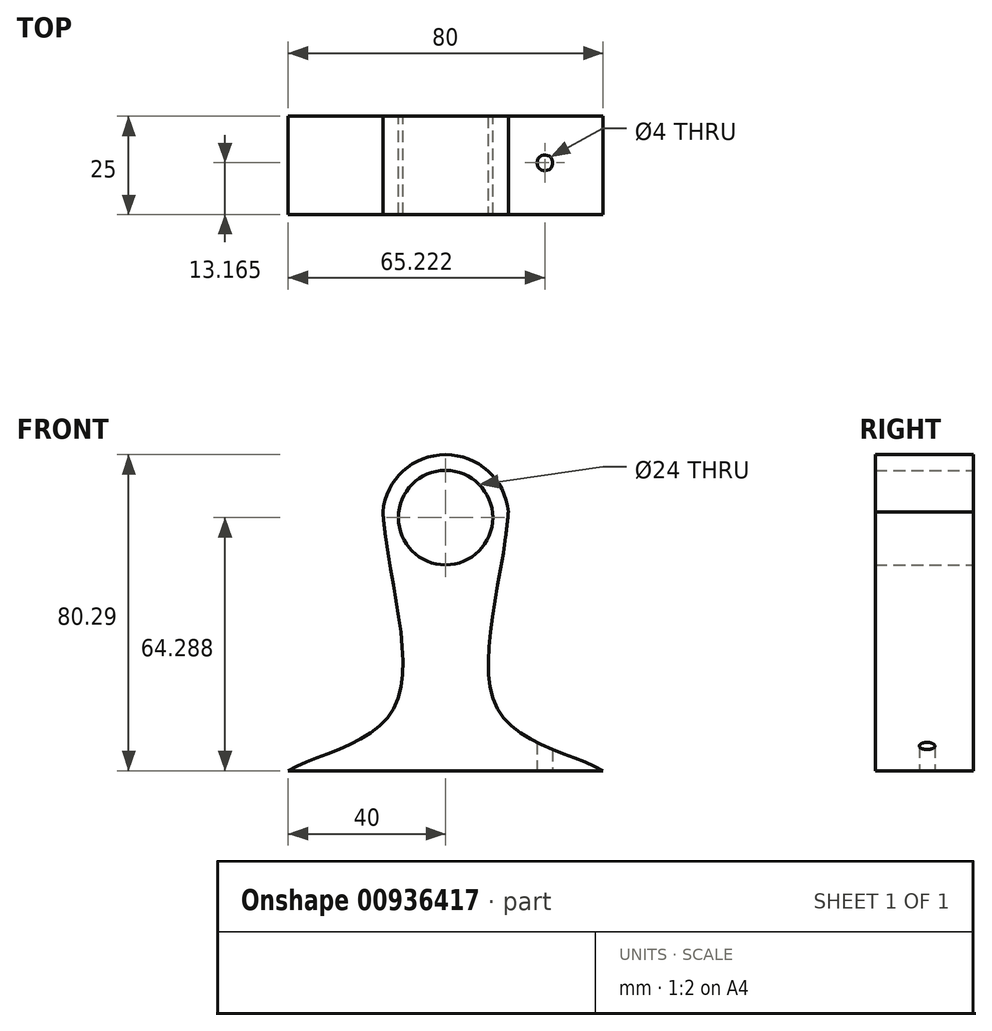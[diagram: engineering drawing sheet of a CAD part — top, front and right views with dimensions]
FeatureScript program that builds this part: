
annotation { "Feature Type Name" : "Feature", "Feature Type Description" : "" }
export const myFeature = defineFeature(function(context is Context, id is Id, definition is map)
    precondition{}
    {
        {
            var Q0;
            Q0=qCreatedBy(makeId("Front.planeOp"),FACE);
            var sketch = newSketch(context, id + "F0", { "sketchPlane" : qUnion([Q0])});
            skCircle(sketch, "E0", {"center": v(0, 64.29) * mm, "radius": 16 * mm});
            skLineSegment(sketch, "E1", {"start": v(0, 0) * mm, "end": v(-40, 0) * mm});
            skCircle(sketch, "E2", {"center": v(0, 64.29) * mm, "radius": 12 * mm});
            skFitSpline(sketch, "E3", {"points": [v(-15.93, 65.8) * mm, v(-13.58, 15.06) * mm, v(-40, 0) * mm], "startDerivative": vector(7.12, -97.73) * mm, "endDerivative": vector(-49.15, -28.34) * mm});
            skFitSpline(sketch, "E4.MirrorCS", {"points": [v(15.93, 65.8) * mm, v(13.58, 15.06) * mm, v(40, 0) * mm], "startDerivative": vector(-7.12, -97.73) * mm, "endDerivative": vector(49.15, -28.34) * mm});
            skLineSegment(sketch, "E5.MirrorCS", {"start": v(0, 0) * mm, "end": v(40, 0) * mm});
            skSolve(sketch);
        }
        {
            var Q0;
            {var subQ4=sQuery(id+"F0.wireOp",EDGE,"E1");Q0=makeQuery(id+"F0.imprint","IMPRINT",FACE,{"disambiguationData":[TD([[makeQuery(id+"F0.imprint","IMPRINT",EDGE,{"derivedFrom":subQ4}),-1.0]])]});}
            var Q1;
            Q1=makeQuery(id+"F0.imprint","IMPRINT",FACE,{"disambiguationData":[TD([[makeQuery(id+"F0.imprint","IMPRINT",EDGE,{"derivedFrom":sQuery(id+"F0.wireOp",EDGE,"E2")}),-1.0]])]});
            extrude(context, id + "F1", {"entities" : qUnion([Q0, Q1]), "depth" : 25 * mm, "offsetDistance" : 25 * mm});
        }
        {
            var Q0;
            Q0=qCreatedBy(makeId("Top.planeOp"),FACE);
            var sketch = newSketch(context, id + "F2", { "sketchPlane" : qUnion([Q0])});
            skCircle(sketch, "E6", {"center": v(25.22, -11.84) * mm, "radius": 2 * mm});
            skCircle(sketch, "E7.MirrorC", {"center": v(-25.22, -11.84) * mm, "radius": 2 * mm});
            skSolve(sketch);
        }
        {
            var Q0;
            Q0=makeQuery(id+"F2.imprint","IMPRINT",FACE,{"disambiguationData":[TD([[makeQuery(id+"F2.imprint","IMPRINT",EDGE,{"derivedFrom":sQuery(id+"F2.wireOp",EDGE,"E6")}),1.0]])]});
            var Q1;
            Q1=makeQuery(id+"F2.imprint","IMPRINT",FACE,{"disambiguationData":[TD([[makeQuery(id+"F2.imprint","IMPRINT",EDGE,{"derivedFrom":sQuery(id+"F2.wireOp",EDGE,"E7.MirrorC")}),-1.0]])]});
            extrude(context, id + "F3", {"entities" : qUnion([Q0, Q1]), "operationType" : NewBodyOperationType.REMOVE, "depth" : 62.5 * mm, "offsetDistance" : 25 * mm});
        }
    });
